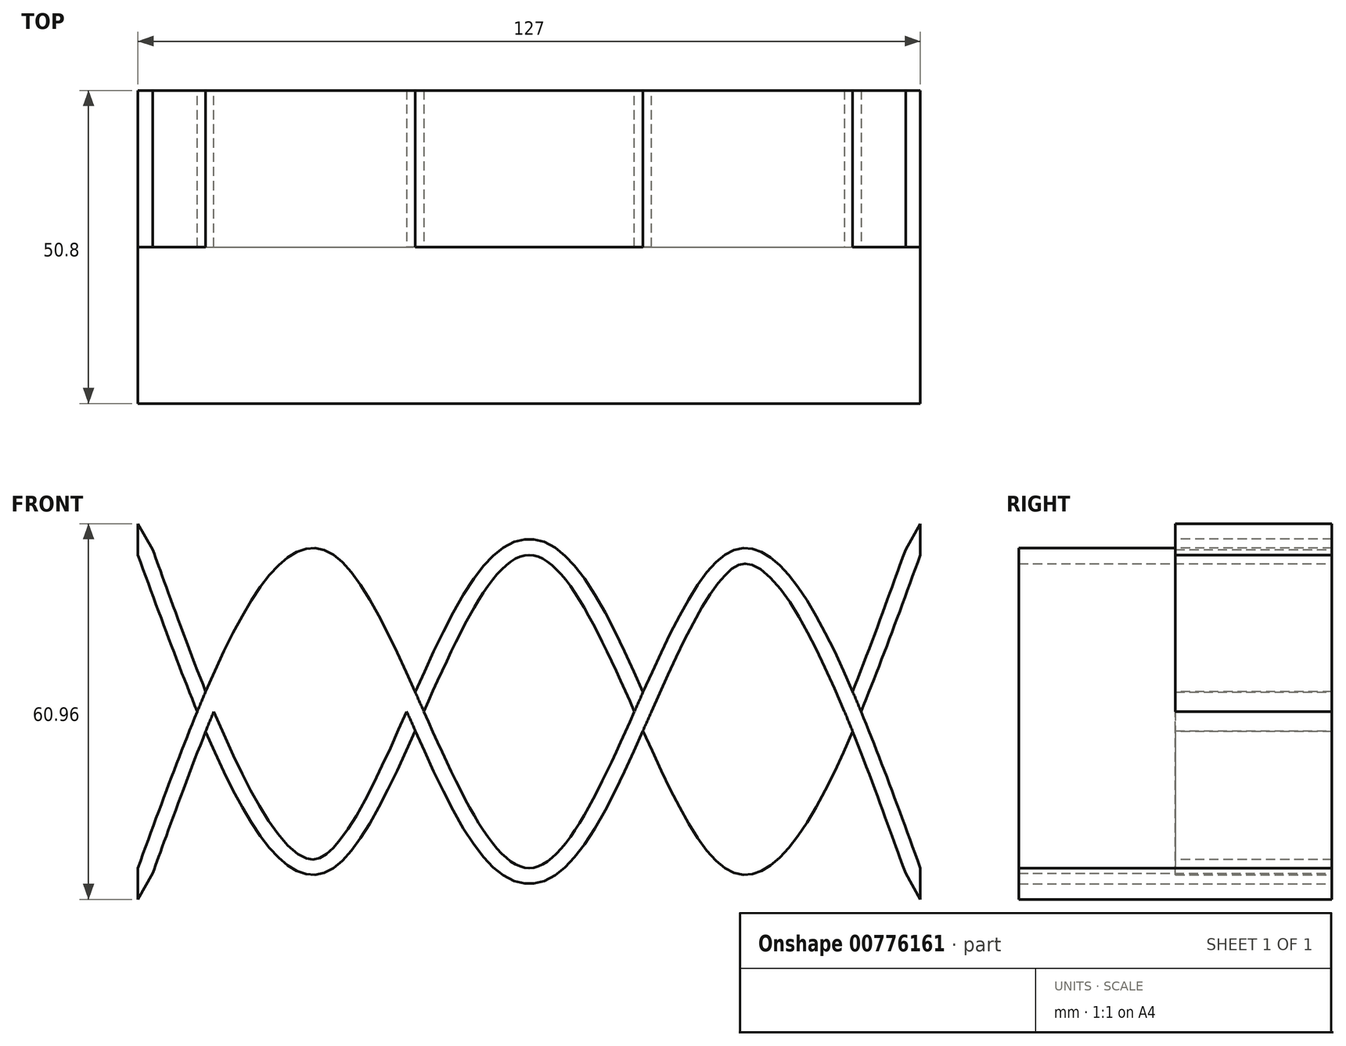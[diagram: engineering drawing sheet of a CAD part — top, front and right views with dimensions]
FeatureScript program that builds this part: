
annotation { "Feature Type Name" : "Feature", "Feature Type Description" : "" }
export const myFeature = defineFeature(function(context is Context, id is Id, definition is map)
    precondition{}
    {
        {
            var Q0;
            Q0=qCreatedBy(makeId("Front.planeOp"),FACE);
            var sketch = newSketch(context, id + "F0", { "sketchPlane" : qUnion([Q0])});
            skLineSegment(sketch, "E0", {"start": v(-63.5, 50.8) * mm, "end": v(-63.5, 0) * mm});
            skLineSegment(sketch, "E1", {"start": v(-127, 0) * mm, "end": v(-127, -5.08) * mm});
            skFitSpline(sketch, "E2", {"points": [v(-127, 0) * mm, v(-95.25, 50.8) * mm, v(-63.5, 0) * mm, v(-31.75, 50.8) * mm, v(0, 0) * mm], "startDerivative": vector(127, 348.34) * mm, "endDerivative": vector(127, -348.34) * mm});
            skFitSpline(sketch, "E3.0", {"points": [v(-124.61, -0.87) * mm, v(-123.3, 2.76) * mm, v(-120.65, 10) * mm, v(-116.7, 20.42) * mm, v(-113.42, 28.35) * mm, v(-110.82, 34.03) * mm, v(-108.88, 37.9) * mm, v(-106.96, 41.3) * mm, v(-105.08, 44.2) * mm, v(-103.26, 46.5) * mm, v(-101.55, 48.15) * mm, v(-100.3, 48.95) * mm, v(-99.46, 49.27) * mm, v(-98.91, 49.39) * mm, v(-98.41, 49.4) * mm, v(-97.9, 49.31) * mm, v(-97.34, 49.1) * mm, v(-96.7, 48.74) * mm, v(-95.96, 48.16) * mm, v(-95.14, 47.35) * mm, v(-94.27, 46.32) * mm, v(-93.06, 44.7) * mm, v(-91.5, 42.23) * mm, v(-89.57, 38.7) * mm, v(-87.62, 34.76) * mm, v(-85.66, 30.51) * mm, v(-83.68, 26.1) * mm, v(-81.7, 21.63) * mm, v(-79.7, 17.22) * mm, v(-77.69, 12.99) * mm, v(-75.66, 9.04) * mm, v(-73.6, 5.48) * mm, v(-71.83, 2.92) * mm, v(-70.35, 1.15) * mm, v(-69.2, -0.02) * mm, v(-67.96, -1.03) * mm, v(-66.62, -1.84) * mm, v(-65.38, -2.3) * mm, v(-64.32, -2.5) * mm, v(-63.5, -2.56) * mm, v(-62.68, -2.5) * mm, v(-61.62, -2.3) * mm, v(-60.38, -1.84) * mm, v(-59.04, -1.03) * mm, v(-57.8, -0.02) * mm, v(-56.65, 1.15) * mm, v(-55.17, 2.92) * mm, v(-53.4, 5.48) * mm, v(-51.34, 9.04) * mm, v(-49.31, 12.99) * mm, v(-47.3, 17.22) * mm, v(-45.3, 21.63) * mm, v(-43.32, 26.1) * mm, v(-41.34, 30.51) * mm, v(-39.38, 34.76) * mm, v(-37.43, 38.7) * mm, v(-35.5, 42.23) * mm, v(-33.94, 44.7) * mm, v(-32.73, 46.32) * mm, v(-31.86, 47.35) * mm, v(-31.04, 48.16) * mm, v(-30.3, 48.74) * mm, v(-29.66, 49.1) * mm, v(-29.1, 49.31) * mm, v(-28.59, 49.4) * mm, v(-28.09, 49.39) * mm, v(-27.54, 49.27) * mm, v(-26.7, 48.95) * mm, v(-25.45, 48.15) * mm, v(-23.74, 46.5) * mm, v(-21.92, 44.2) * mm, v(-20.04, 41.3) * mm, v(-18.12, 37.9) * mm, v(-16.18, 34.03) * mm, v(-13.58, 28.35) * mm, v(-10.3, 20.42) * mm, v(-6.35, 10) * mm, v(-3.7, 2.76) * mm, v(-2.39, -0.87) * mm]});
            skLineSegment(sketch, "E4", {"start": v(-127, -5.08) * mm, "end": v(-124.61, -0.87) * mm});
            skLineSegment(sketch, "E5", {"start": v(-2.39, -0.87) * mm, "end": v(0, -5.08) * mm});
            skLineSegment(sketch, "E6", {"start": v(0, 0) * mm, "end": v(0, -5.08) * mm});
            skFitSpline(sketch, "E7.MirrorCS", {"points": [v(-127, 50.8) * mm, v(-95.25, 0) * mm, v(-63.5, 50.8) * mm, v(-31.75, 0) * mm, v(0, 50.8) * mm], "startDerivative": vector(127, -348.34) * mm, "endDerivative": vector(127, 348.34) * mm});
            skLineSegment(sketch, "E8.MirrorCS", {"start": v(-127, 50.8) * mm, "end": v(-127, 55.88) * mm});
            skLineSegment(sketch, "E9.MirrorCS", {"start": v(-127, 55.88) * mm, "end": v(-124.61, 51.67) * mm});
            skFitSpline(sketch, "E10.MirrorCS", {"points": [v(-127, 0) * mm, v(-95.25, 50.8) * mm, v(-63.5, 0) * mm, v(-31.75, 50.8) * mm, v(0, 0) * mm], "startDerivative": vector(127, 348.34) * mm, "endDerivative": vector(127, -348.34) * mm});
            skLineSegment(sketch, "E11.MirrorCS", {"start": v(0, 50.8) * mm, "end": v(0, 55.88) * mm});
            skLineSegment(sketch, "E12.MirrorCS", {"start": v(-2.39, 51.67) * mm, "end": v(0, 55.88) * mm});
            skFitSpline(sketch, "E13.0", {"points": [v(-124.61, 51.67) * mm, v(-123.3, 48.04) * mm, v(-120.65, 40.8) * mm, v(-116.7, 30.38) * mm, v(-113.42, 22.45) * mm, v(-110.82, 16.77) * mm, v(-108.88, 12.9) * mm, v(-106.96, 9.5) * mm, v(-105.08, 6.6) * mm, v(-103.26, 4.3) * mm, v(-101.55, 2.65) * mm, v(-100.3, 1.85) * mm, v(-99.46, 1.53) * mm, v(-98.91, 1.41) * mm, v(-98.41, 1.4) * mm, v(-97.9, 1.49) * mm, v(-97.34, 1.7) * mm, v(-96.7, 2.06) * mm, v(-95.96, 2.64) * mm, v(-95.14, 3.45) * mm, v(-94.27, 4.48) * mm, v(-93.06, 6.1) * mm, v(-91.5, 8.57) * mm, v(-89.57, 12.1) * mm, v(-87.62, 16.04) * mm, v(-85.66, 20.29) * mm, v(-83.68, 24.7) * mm, v(-81.7, 29.17) * mm, v(-79.7, 33.58) * mm, v(-77.69, 37.81) * mm, v(-75.66, 41.76) * mm, v(-73.6, 45.32) * mm, v(-71.83, 47.88) * mm, v(-70.35, 49.65) * mm, v(-69.2, 50.82) * mm, v(-67.96, 51.83) * mm, v(-66.62, 52.64) * mm, v(-65.38, 53.1) * mm, v(-64.32, 53.3) * mm, v(-63.5, 53.36) * mm, v(-62.68, 53.3) * mm, v(-61.62, 53.1) * mm, v(-60.38, 52.64) * mm, v(-59.04, 51.83) * mm, v(-57.8, 50.82) * mm, v(-56.65, 49.65) * mm, v(-55.17, 47.88) * mm, v(-53.4, 45.32) * mm, v(-51.34, 41.76) * mm, v(-49.31, 37.81) * mm, v(-47.3, 33.58) * mm, v(-45.3, 29.17) * mm, v(-43.32, 24.7) * mm, v(-41.34, 20.29) * mm, v(-39.38, 16.04) * mm, v(-37.43, 12.1) * mm, v(-35.5, 8.57) * mm, v(-33.94, 6.1) * mm, v(-32.73, 4.48) * mm, v(-31.86, 3.45) * mm, v(-31.04, 2.64) * mm, v(-30.3, 2.06) * mm, v(-29.66, 1.7) * mm, v(-29.1, 1.49) * mm, v(-28.59, 1.4) * mm, v(-28.09, 1.41) * mm, v(-27.54, 1.53) * mm, v(-26.7, 1.85) * mm, v(-25.45, 2.65) * mm, v(-23.74, 4.3) * mm, v(-21.92, 6.6) * mm, v(-20.04, 9.5) * mm, v(-18.12, 12.9) * mm, v(-16.18, 16.77) * mm, v(-13.58, 22.45) * mm, v(-10.3, 30.38) * mm, v(-6.35, 40.8) * mm, v(-3.7, 48.04) * mm, v(-2.39, 51.67) * mm]});
            skSolve(sketch);
        }
        {
            var Q0;
            {var subQ6=sQuery(id+"F0.wireOp",EDGE,"E8.MirrorCS");Q0=makeQuery(id+"F0.imprint","IMPRINT",FACE,{"disambiguationData":[TD([[makeQuery(id+"F0.imprint","IMPRINT",EDGE,{"derivedFrom":subQ6}),-1.0]])]});}
            var Q1;
            {var subQ0=sQuery(id+"F0.wireOp",EDGE,"E7.MirrorCS");var subQ1=sQuery(id+"F0.wireOp",EDGE,"E3.0");var subQ2=makeQuery(id+"F0.imprint","INTERSECT",VERTEX,{"disambiguationData":[OD(0.0)],"derivedFrom":[subQ1,subQ0]});Q1=makeQuery(id+"F0.imprint","IMPRINT",FACE,{"disambiguationData":[TD([[makeQuery(id+"F0.imprint","IMPRINT",EDGE,{"disambiguationData":[TD([[subQ2,-1.0]])],"derivedFrom":subQ1}),-1.0]])]});}
            var Q2;
            {var subQ3=sQuery(id+"F0.wireOp",EDGE,"E7.MirrorCS");var subQ7=makeQuery(id+"F0.imprint","INTERSECT",VERTEX,{"derivedFrom":[sQuery(id+"F0.wireOp",EDGE,"E0"),subQ3]});Q2=makeQuery(id+"F0.imprint","IMPRINT",FACE,{"disambiguationData":[TD([[makeQuery(id+"F0.imprint","IMPRINT",EDGE,{"disambiguationData":[TD([[subQ7,1.0]])],"derivedFrom":subQ3}),1.0]])]});}
            var Q3;
            {var subQ0=sQuery(id+"F0.wireOp",EDGE,"E7.MirrorCS");var subQ1=sQuery(id+"F0.wireOp",EDGE,"E3.0");var subQ2=makeQuery(id+"F0.imprint","INTERSECT",VERTEX,{"disambiguationData":[OD(2.0)],"derivedFrom":[subQ1,subQ0]});Q3=makeQuery(id+"F0.imprint","IMPRINT",FACE,{"disambiguationData":[TD([[makeQuery(id+"F0.imprint","IMPRINT",EDGE,{"disambiguationData":[TD([[subQ2,-1.0]])],"derivedFrom":subQ1}),-1.0]])]});}
            var Q4;
            {var subQ1=sQuery(id+"F0.wireOp",EDGE,"E11.MirrorCS");Q4=makeQuery(id+"F0.imprint","IMPRINT",FACE,{"disambiguationData":[TD([[makeQuery(id+"F0.imprint","IMPRINT",EDGE,{"derivedFrom":subQ1}),1.0]])]});}
            extrude(context, id + "F1", {"entities" : qUnion([Q0, Q1, Q2, Q3, Q4]), "depth" : 25.4 * mm, "offsetDistance" : 25.4 * mm});
        }
        {
            var Q0;
            {var subQ5=sQuery(id+"F0.wireOp",EDGE,"E1");Q0=makeQuery(id+"F0.imprint","IMPRINT",FACE,{"disambiguationData":[TD([[makeQuery(id+"F0.imprint","IMPRINT",EDGE,{"derivedFrom":subQ5}),1.0]])]});}
            var Q1;
            {var subQ0=sQuery(id+"F0.wireOp",EDGE,"E7.MirrorCS");var subQ1=sQuery(id+"F0.wireOp",EDGE,"E3.0");var subQ2=makeQuery(id+"F0.imprint","INTERSECT",VERTEX,{"disambiguationData":[OD(0.0)],"derivedFrom":[subQ1,subQ0]});Q1=makeQuery(id+"F0.imprint","IMPRINT",FACE,{"disambiguationData":[TD([[makeQuery(id+"F0.imprint","IMPRINT",EDGE,{"disambiguationData":[TD([[subQ2,-1.0]])],"derivedFrom":subQ1}),1.0]])]});}
            var Q2;
            {var subQ0=sQuery(id+"F0.wireOp",EDGE,"E13.0");var subQ1=sQuery(id+"F0.wireOp",EDGE,"E3.0");var subQ2=makeQuery(id+"F0.imprint","INTERSECT",VERTEX,{"disambiguationData":[OD(0.0)],"derivedFrom":[subQ1,subQ0]});Q2=makeQuery(id+"F0.imprint","IMPRINT",FACE,{"disambiguationData":[TD([[makeQuery(id+"F0.imprint","IMPRINT",EDGE,{"disambiguationData":[TD([[subQ2,-1.0]])],"derivedFrom":subQ1}),1.0]])]});}
            var Q3;
            {var subQ0=sQuery(id+"F0.wireOp",EDGE,"E7.MirrorCS");var subQ1=sQuery(id+"F0.wireOp",EDGE,"E3.0");var subQ2=makeQuery(id+"F0.imprint","INTERSECT",VERTEX,{"disambiguationData":[OD(1.0)],"derivedFrom":[subQ1,subQ0]});Q3=makeQuery(id+"F0.imprint","IMPRINT",FACE,{"disambiguationData":[TD([[makeQuery(id+"F0.imprint","IMPRINT",EDGE,{"disambiguationData":[TD([[subQ2,1.0]])],"derivedFrom":subQ1}),1.0]])]});}
            var Q4;
            {var subQ2=sQuery(id+"F0.wireOp",EDGE,"E7.MirrorCS");var subQ4=sQuery(id+"F0.wireOp",EDGE,"E3.0");var subQ7=makeQuery(id+"F0.imprint","INTERSECT",VERTEX,{"disambiguationData":[OD(1.0)],"derivedFrom":[subQ4,subQ2]});Q4=makeQuery(id+"F0.imprint","IMPRINT",FACE,{"disambiguationData":[TD([[makeQuery(id+"F0.imprint","IMPRINT",EDGE,{"disambiguationData":[TD([[subQ7,-1.0]])],"derivedFrom":subQ4}),1.0]])]});}
            var Q5;
            {var subQ0=sQuery(id+"F0.wireOp",EDGE,"E7.MirrorCS");var subQ1=sQuery(id+"F0.wireOp",EDGE,"E3.0");var subQ2=makeQuery(id+"F0.imprint","INTERSECT",VERTEX,{"disambiguationData":[OD(2.0)],"derivedFrom":[subQ1,subQ0]});Q5=makeQuery(id+"F0.imprint","IMPRINT",FACE,{"disambiguationData":[TD([[makeQuery(id+"F0.imprint","IMPRINT",EDGE,{"disambiguationData":[TD([[subQ2,-1.0]])],"derivedFrom":subQ1}),1.0]])]});}
            var Q6;
            {var subQ0=sQuery(id+"F0.wireOp",EDGE,"E13.0");var subQ1=sQuery(id+"F0.wireOp",EDGE,"E3.0");var subQ2=makeQuery(id+"F0.imprint","INTERSECT",VERTEX,{"disambiguationData":[OD(2.0)],"derivedFrom":[subQ1,subQ0]});Q6=makeQuery(id+"F0.imprint","IMPRINT",FACE,{"disambiguationData":[TD([[makeQuery(id+"F0.imprint","IMPRINT",EDGE,{"disambiguationData":[TD([[subQ2,-1.0]])],"derivedFrom":subQ1}),1.0]])]});}
            var Q7;
            {var subQ0=sQuery(id+"F0.wireOp",EDGE,"E7.MirrorCS");var subQ1=sQuery(id+"F0.wireOp",EDGE,"E3.0");var subQ2=makeQuery(id+"F0.imprint","INTERSECT",VERTEX,{"disambiguationData":[OD(3.0)],"derivedFrom":[subQ1,subQ0]});Q7=makeQuery(id+"F0.imprint","IMPRINT",FACE,{"disambiguationData":[TD([[makeQuery(id+"F0.imprint","IMPRINT",EDGE,{"disambiguationData":[TD([[subQ2,1.0]])],"derivedFrom":subQ1}),1.0]])]});}
            var Q8;
            {var subQ6=sQuery(id+"F0.wireOp",EDGE,"E5");Q8=makeQuery(id+"F0.imprint","IMPRINT",FACE,{"disambiguationData":[TD([[makeQuery(id+"F0.imprint","IMPRINT",EDGE,{"derivedFrom":subQ6}),1.0]])]});}
            extrude(context, id + "F2", {"entities" : qUnion([Q0, Q1, Q2, Q3, Q4, Q5, Q6, Q7, Q8]), "depth" : 50.8 * mm, "offsetDistance" : 25.4 * mm});
        }
    });
